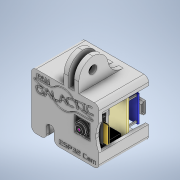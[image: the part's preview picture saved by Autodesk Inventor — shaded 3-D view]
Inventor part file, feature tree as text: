
AUTODESK INVENTOR PART (.ipt)
format: ipt  version: 2022 (Build 260153000, 153)  size: 1,458,688 bytes
history: native  units: in
note: dims shown in document units (in); Inventor stores cm internally (conversion verified against a paired STEP export)
features: extrude x31, sketch x30, fillet x4, chamfer x2, other x1
ambient origin geometry x8: Origin, YZ Plane, XZ Plane, XY Plane, X Axis, Y Axis, Z Axis, Center Point
bodies: Solid1 (feature_tree), Solid2 (feature_tree), Solid3 (feature_tree), Solid4 (feature_tree), Solid5 (feature_tree), Solid6 (feature_tree), Solid7 (feature_tree), Solid8 (feature_tree), Solid9 (feature_tree), Solid10 (feature_tree), Solid11 (feature_tree), Solid12 (feature_tree), Solid13 (feature_tree), Solid14 (feature_tree)
feature tree (68):
  extrude  "Extrusion1"  Depth=1.065in
  extrude  "Extrusion2"  Depth=0.7795in
  extrude  "Extrusion3"  Depth=0.0787in TaperAngle=0.0deg
  extrude  "Extrusion4"  Depth=0.2307in
  extrude  "Extrusion5"  Depth=0.0787in TaperAngle=0.0deg
  extrude  "Extrusion6"  Depth=0.1339in
  chamfer  "Chamfer1"  Distance=0.1476in
  extrude  "Extrusion7"  Depth=0.315in
  fillet  "Fillet2"  Radius=0.1575in
  extrude  "Extrusion8"  Depth=0.3217in
  extrude  "Extrusion9"  Depth=0.248in
  fillet  "Fillet3"  Radius=0.0512in
  extrude  "Extrusion10"  Depth=0.0394in TaperAngle=0.0deg
  extrude  "Extrusion11"  Depth=0.0787in
  extrude  "Extrusion12"  Depth=0.0315in
  fillet  "Fillet4"  Radius=0.0315in
  extrude  "Extrusion13"  Depth=0.0079in
  extrude  "Extrusion14"  Depth=0.4724in TaperAngle=0.0deg
  extrude  "Extrusion15"  Depth=0.0394in
  extrude  "Extrusion16"  Depth=0.0134in
  extrude  "Extrusion17"  Depth=0.5906in TaperAngle=0.0deg
  extrude  "Extrusion18"  Depth=0.0197in
  extrude  "Extrusion19"  Depth=0.7969in
  extrude  "Extrusion20"  Depth=0.0413in
  extrude  "Extrusion21"  Depth=0.6189in
  extrude  "Extrusion22"  Depth=0.0276in
  extrude  "Extrusion23"  Depth=0.1551in
  extrude  "Extrusion24"  Depth=0.0512in TaperAngle=0.0deg
  extrude  "Extrusion25"  Depth=0.0807in
  extrude  "Extrusion26"  Depth=0.0583in
  extrude  "Extrusion27"  Depth=0.0118in TaperAngle=0.0deg
  chamfer  "Chamfer2"  Distance=1.5472in
  extrude  "Extrusion28"  Depth=0.3937in
  extrude  "Extrusion29"  Depth=0.3937in
  fillet  "Fillet5"  Radius=0.1378in
  extrude  "Extrusion30"  Depth=0.3937in
  extrude  "Extrusion31"  Depth=0.3937in
  sketch  "Sketch1"  dims[d0=1.5591in d1=1.065in]
  sketch  "Sketch2"  dims[d2=0.5325in d3=0.7795in]
  sketch  "Sketch3"  dims[d4=0.0787in d5=0.063in d6=0.0in]
  sketch  "Sketch4"  dims[d7=0.5882in d8=0.2307in]
  sketch  "Sketch5"  dims[d9=0.2449in d10=0.0787in d11=0.0in]
  sketch  "Sketch6"  dims[d12=0.1339in d13=0.1339in]
  sketch  "Sketch7"  dims[d14=0.1811in]
  sketch  "Sketch8"  dims[d15=0.315in d16=0.1476in d17=0.0in]
  sketch  "Sketch9"  dims[d18=0.3098in d19=0.315in d20=0.1575in]
  sketch  "Sketch10"  dims[d21=0.1608in d22=0.3217in]
  sketch  "Sketch11"  dims[d23=0.0709in d24=0.0in d25=0.248in d26=0.0512in d27=0.0in]
  sketch  "Sketch12"  dims[d28=0.0669in d29=0.0394in d30=0.0in]
  sketch  "Sketch13"  dims[d31=0.0394in d32=0.0787in d33=45.0deg d35=0.0004in]
  sketch  "Sketch14"  dims[d36=0.0394in d37=0.0in d38=0.0315in d39=0.0315in]
  sketch  "Sketch15"  dims[d40=0.0079in d41=0.0972in]
  sketch  "Sketch16"  dims[d42=0.0472in d43=0.4724in d44=0.0in]
  sketch  "Sketch17"  dims[d45=0.4339in d46=0.0394in]
  sketch  "Sketch18"  dims[d47=0.0039in d48=0.0134in]
  sketch  "Sketch19"  dims[d49=0.0134in d50=0.5906in d51=0.0in]
  sketch  "Sketch20"  dims[d52=0.0197in d53=0.0937in]
  sketch  "Sketch21"  dims[d54=0.0937in d55=0.7969in]
  sketch  "Sketch22"  dims[d56=0.0394in d57=0.0413in]
  other  "Case Part A"
  sketch  "Sketch23"  dims[d58=0.1339in d59=0.6189in]
  sketch  "Sketch24"  dims[d60=0.4594in d61=0.0in d62=0.0276in]
  sketch  "Sketch26"  dims[d63=0.189in d64=0.1551in]
  sketch  "Sketch27"  dims[d65=0.2717in d66=0.0512in d67=0.0in]
  sketch  "Sketch28"  dims[d68=0.0693in d69=0.0807in]
  sketch  "Sketch29"  dims[d70=0.1614in d71=0.0583in]
  sketch  "Sketch30"  dims[d72=0.1165in d73=0.0118in d74=0.0in]
  sketch  "Sketch32"  dims[d75=0.0079in d76=1.5472in d77=1.2654in d78=0.1433in d79=0.1378in d80=0.0059in d81=0.0059in d82=0.0618in d83=0.0in d84=0.0394in d85=0.1465in d86=0.0039in d87=0.6693in d88=0.4362in d89=0.0in d90=0.2972in d91=0.2244in d94=0.4724in d95=0.0in d96=0.0335in d97=0.0335in d98=0.0335in d99=0.0335in d100=0.0335in d101=0.0335in d102=0.0335in d103=0.0157in d104=0.5472in d105=0.2697in d106=0.9016in d107=0.2252in d108=0.0in d109=0.6713in d110=0.0276in d111=0.3539in d112=1.0965in d113=0.4587in d114=0.0366in d115=0.0in d116=0.2961in d117=0.2142in d118=0.0512in d119=0.1876in d120=0.1876in d121=0.1098in d122=0.0in d125=0.2134in d126=0.0551in d127=0.0413in d128=0.0413in d129=0.0in d130=0.0in d131=0.0157in d132=0.0157in d133=0.0157in d134=0.0157in d135=0.0157in d136=0.0157in d137=0.0157in d138=0.0157in d139=0.2062in d140=0.0in d141=0.1181in d142=0.1181in d143=0.3406in d144=0.0358in d145=0.0335in d146=0.0in d147=0.065in d148=0.1969in d149=0.1969in d150=0.1969in d151=0.1969in d152=0.0197in d153=0.0197in d154=0.0197in d155=0.0197in d156=0.0197in d157=0.0197in d158=0.0197in d159=0.0197in d160=0.1772in d161=0.0in d162=0.0394in d163=0.0394in d164=0.0394in d166=0.0394in d168=0.0in d169=0.0787in d171=0.0787in d172=0.0394in d173=0.0394in d174=0.0394in d175=0.0787in d176=0.0394in d177=0.0394in d178=0.0394in d179=0.0394in d180=0.3799in d181=0.374in d182=0.3937in d183=0.7087in d184=0.0787in d185=0.0787in d186=0.1181in d187=0.1181in d188=0.0787in d189=0.0787in d190=0.0in d191=0.0079in d192=0.0079in d193=0.0079in d194=0.0079in d195=0.0in d198=0.0in d199=0.0in d201=0.0in d202=0.0in d203=0.0787in d204=0.0in d205=0.1181in d206=0.0079in d207=0.0079in d208=0.0768in d211=0.1181in d212=0.0079in d213=0.1181in d214=0.0709in d215=0.1082in d216=0.0079in d217=0.1181in d218=0.1082in d219=0.0709in d220=0.4564in d221=0.3701in d222=1.1811in d223=0.0in d224=0.0079in d225=0.0197in d226=0.3543in d227=0.0787in d228=0.0in d229=0.0197in d230=0.0787in d231=0.0in d232=0.0787in d233=0.3543in d234=0.4724in d235=0.0394in d236=0.0in d237=0.3543in d238=0.0394in d239=45.0deg d240=0.748in d241=0.1181in d242=0.1181in d243=0.1417in d244=0.3937in d245=0.6535in d246=0.0in d247=0.2067in d248=0.2992in d249=0.748in d250=0.3543in d251=0.0in d252=0.0in d253=0.3937in d254=0.0394in d255=0.0in d256=0.0394in d257=0.0in]
